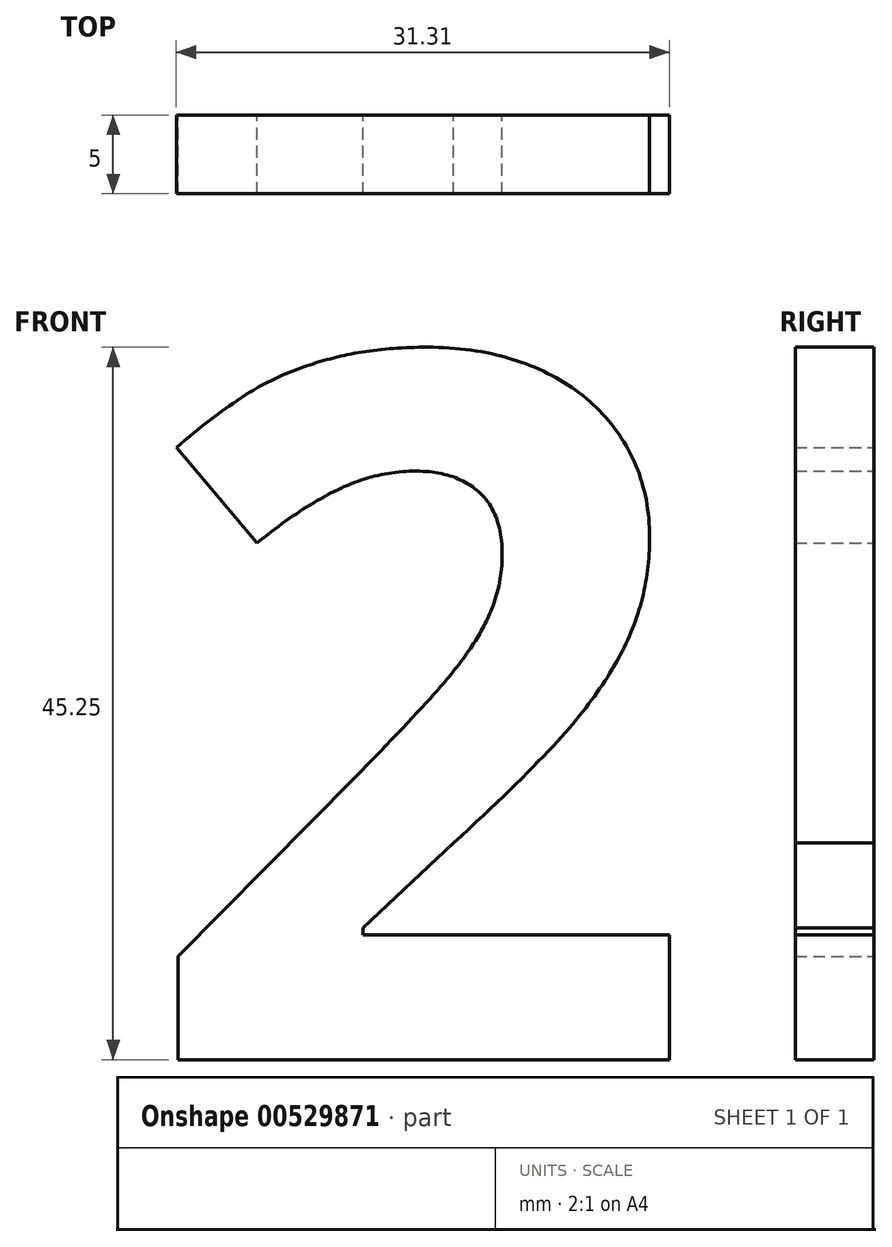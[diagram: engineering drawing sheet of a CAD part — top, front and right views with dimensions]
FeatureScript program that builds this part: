
annotation { "Feature Type Name" : "Feature", "Feature Type Description" : "" }
export const myFeature = defineFeature(function(context is Context, id is Id, definition is map)
    precondition{}
    {
        {
            var Q0;
            Q0=qCreatedBy(makeId("Front.planeOp"),FACE);
            var sketch = newSketch(context, id + "F0", { "sketchPlane" : qUnion([Q0])});
            skText(sketch, "E0", { "text": "2", "fontName": "OpenSans-Bold.ttf"});
            const initialGuessF0  = {"E0": [-0.0491, 0.01137, 1, 0, 0.045]};
            skSetInitialGuess(sketch, initialGuessF0);
            skSolve(sketch);
        }
        {
            var Q0;
            Q0=makeQuery(id+"F0.imprint","IMPRINT",FACE,{"disambiguationData":[TD([[makeQuery(id+"F0.imprint","IMPRINT",EDGE,{"derivedFrom":sQuery(id+"F0.wireOp",EDGE,"E0.sketch_text.stroke-0")}),-1.0]])]});
            extrude(context, id + "F1", {"entities" : qUnion([Q0]), "depth" : 5 * mm, "offsetDistance" : 25 * mm});
        }
    });
